# Revit family: SIGNUM Halter LP50
name_source: partatom
category: HLS-Bauteile
units: mm (PartAtom-declared; Revit-internal decimal feet)

## family parameters
Arbeitsebenenbasiert = Ja
Beim Laden mit Abzugskörper schneiden = Nein
Bemaßung runder Anschluss = Durchmesser verwenden
Beschriftungsausrichtung beibehalten = Nein
Gemeinsam genutzt = Ja
Immer vertikal = Nein
Klassifizierung = Keine
Raumberechnungspunkt = Nein
Teiletyp = Normal

## types (1)
- SIGNUM Halter LP50
    Artikelnummer = 0812037
    Breite Platte = 40 mm  [stored 0.131234 ft]
    EAN = 4250928467546
    Fabrikat = MEFA
    Gewicht = 0,31 kg
    Gewicht pro Bauteil = 0,31 kg
    Kurztext1 = SIGNUM Halter LP50
    Kurztext2 = für SIGNUM LP50 gvz
    Lochdurchmesser = 11 mm
    Länge Platte = 100 mm  [stored 0.328084 ft]
    Material = Stahl
    Materialname = S235
    Mengeneinheit = St
    Profil = SIGNUM
    Profiltyp = LP50
    Stärke Platte = 4 mm  [stored 0.0131234 ft]
    Vorgabe-Ansicht = 1219 mm
    vpe = 25

note: [stored X ft] marks values corroborated as IEEE doubles in the binary element streams (Revit-internal decimal feet)
